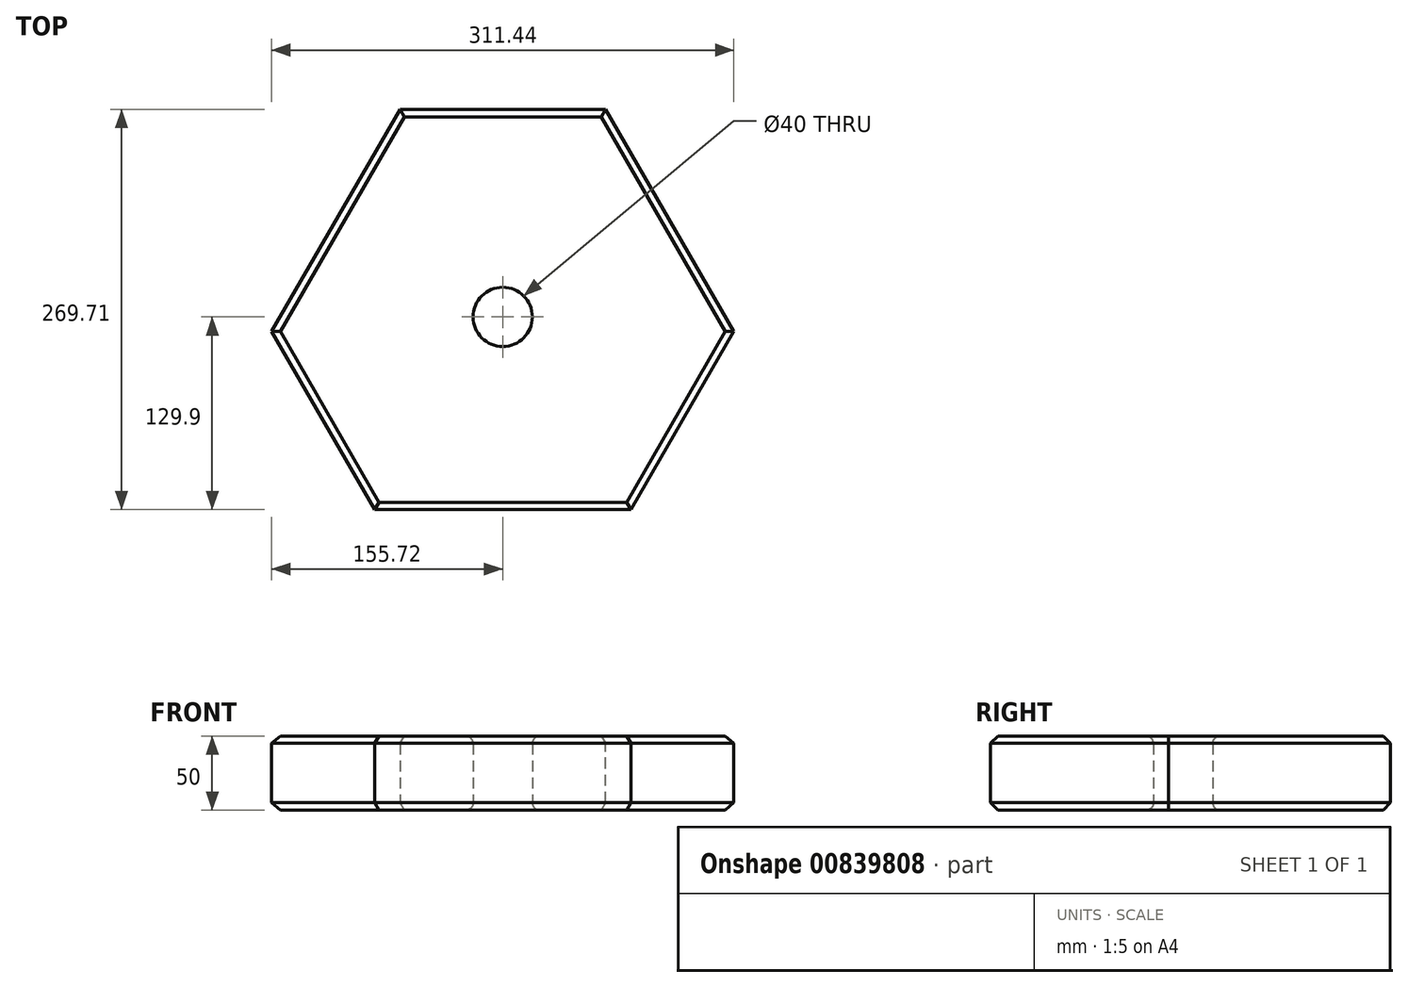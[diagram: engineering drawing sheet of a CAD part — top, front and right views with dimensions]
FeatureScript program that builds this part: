
annotation { "Feature Type Name" : "Feature", "Feature Type Description" : "" }
export const myFeature = defineFeature(function(context is Context, id is Id, definition is map)
    precondition{}
    {
        {
            var Q0;
            Q0=qCreatedBy(makeId("Top.planeOp"),FACE);
            var sketch = newSketch(context, id + "F0", { "sketchPlane" : qUnion([Q0])});
            skLineSegment(sketch, "E0", {"start": v(-225, -92.35) * mm, "end": v(0, 297.36) * mm});
            skLineSegment(sketch, "E1", {"start": v(0, 297.36) * mm, "end": v(225, -92.35) * mm});
            skLineSegment(sketch, "E2", {"start": v(225, -92.35) * mm, "end": v(-225, -92.35) * mm});
            skCircle(sketch, "E3", {"center": v(0, 37.55) * mm, "radius": 20 * mm});
            skPoint(sketch, "E4.orphan", {"position": v(-112.5, 102.5) * mm});
            skPoint(sketch, "E5.orphan", {"position": v(112.5, 102.5) * mm});
            skPoint(sketch, "E6.orphan", {"position": v(0, -92.35) * mm});
            skPoint(sketch, "E7.orphan", {"position": v(56.25, 5.07) * mm});
            skPoint(sketch, "E8.end.orphan", {"position": v(-56.25, 5.07) * mm});
            skPoint(sketch, "E9.end.orphan", {"position": v(0, 102.5) * mm});
            skSolve(sketch);
        }
        {
            var Q0;
            Q0=makeQuery(id+"F0.imprint","IMPRINT",FACE,{"disambiguationData":[TD([[makeQuery(id+"F0.imprint","IMPRINT",EDGE,{"derivedFrom":sQuery(id+"F0.wireOp",EDGE,"E0")}),-1.0]])]});
            extrude(context, id + "F1", {"entities" : qUnion([Q0]), "depth" : 50 * mm, "offsetDistance" : 25 * mm});
        }
        {
            var Q0;
            Q0=makeQuery(id+"F1.opExtrude","SWEPT_EDGE",EDGE,{"disambiguationData":[OSD([sQuery(id+"F0.wireOp",EDGE,"E1"),sQuery(id+"F0.wireOp",EDGE,"E2")])]});
            var Q1;
            Q1=makeQuery(id+"F1.opExtrude","SWEPT_EDGE",EDGE,{"disambiguationData":[OSD([sQuery(id+"F0.wireOp",EDGE,"E0"),sQuery(id+"F0.wireOp",EDGE,"E2")])]});
            var Q2;
            Q2=makeQuery(id+"F1.opExtrude","SWEPT_EDGE",EDGE,{"disambiguationData":[OSD([sQuery(id+"F0.wireOp",EDGE,"E0"),sQuery(id+"F0.wireOp",EDGE,"E1")])]});
            chamfer(context, id + "F2", {"entities" : qUnion([Q0, Q1, Q2]), "width" : 80 * mm, "tangentPropagation" : true});
        }
        {
            var Q0;
            Q0=makeQuery(id+"F1.opExtrude","CAP_EDGE",EDGE,{"disambiguationData":[OSD([sQuery(id+"F0.wireOp",EDGE,"E3")])],"isStart":false});
            var Q1;
            Q1=makeQuery(id+"F1.opExtrude","CAP_EDGE",EDGE,{"disambiguationData":[OSD([sQuery(id+"F0.wireOp",EDGE,"E3")])],"isStart":true});
            fillet(context, id + "F3", {"entities" : qUnion([Q0, Q1]), "radius" : 5 * mm, "tangentPropagation" : true, "allowEdgeOverflow" : false});
        }
        {
            var Q0;
            Q0=makeQuery(id+"F1.opExtrude","CAP_EDGE",EDGE,{"disambiguationData":[OSD([sQuery(id+"F0.wireOp",EDGE,"E1")])],"isStart":false});
            var Q1;
            {var subQ0=sQuery(id+"F0.wireOp",EDGE,"E2");var subQ1=sQuery(id+"F0.wireOp",EDGE,"E1");Q1=makeQuery(id+"F2.opChamfer","BLEND_EDGE",EDGE,{"blendedFrom":[makeQuery(id+"F1.opExtrude","SWEPT_EDGE",EDGE,{"disambiguationData":[OSD([subQ1,subQ0])]}),makeQuery(id+"F1.opExtrude","CAP_FACE",FACE,{"disambiguationData":[OSD([sQuery(id+"F0.wireOp",EDGE,"E0"),subQ1,subQ0,sQuery(id+"F0.wireOp",EDGE,"E3")])],"isStart":false})],"blendedInto":[makeQuery(id+"F1.opExtrude","CAP_FACE",FACE,{"disambiguationData":[OSD([sQuery(id+"F0.wireOp",EDGE,"E0"),subQ1,subQ0,sQuery(id+"F0.wireOp",EDGE,"E3")])],"isStart":false})]});}
            var Q2;
            Q2=makeQuery(id+"F1.opExtrude","CAP_EDGE",EDGE,{"disambiguationData":[OSD([sQuery(id+"F0.wireOp",EDGE,"E2")])],"isStart":false});
            var Q3;
            {var subQ0=sQuery(id+"F0.wireOp",EDGE,"E2");var subQ1=sQuery(id+"F0.wireOp",EDGE,"E0");Q3=makeQuery(id+"F2.opChamfer","BLEND_EDGE",EDGE,{"blendedFrom":[makeQuery(id+"F1.opExtrude","SWEPT_EDGE",EDGE,{"disambiguationData":[OSD([subQ1,subQ0])]}),makeQuery(id+"F1.opExtrude","CAP_FACE",FACE,{"disambiguationData":[OSD([subQ1,sQuery(id+"F0.wireOp",EDGE,"E1"),subQ0,sQuery(id+"F0.wireOp",EDGE,"E3")])],"isStart":false})],"blendedInto":[makeQuery(id+"F1.opExtrude","CAP_FACE",FACE,{"disambiguationData":[OSD([subQ1,sQuery(id+"F0.wireOp",EDGE,"E1"),subQ0,sQuery(id+"F0.wireOp",EDGE,"E3")])],"isStart":false})]});}
            var Q4;
            Q4=makeQuery(id+"F1.opExtrude","CAP_EDGE",EDGE,{"disambiguationData":[OSD([sQuery(id+"F0.wireOp",EDGE,"E0")])],"isStart":false});
            var Q5;
            {var subQ0=sQuery(id+"F0.wireOp",EDGE,"E2");var subQ1=sQuery(id+"F0.wireOp",EDGE,"E1");Q5=makeQuery(id+"F2.opChamfer","BLEND_EDGE",EDGE,{"blendedFrom":[makeQuery(id+"F1.opExtrude","SWEPT_EDGE",EDGE,{"disambiguationData":[OSD([subQ1,subQ0])]}),makeQuery(id+"F1.opExtrude","CAP_FACE",FACE,{"disambiguationData":[OSD([sQuery(id+"F0.wireOp",EDGE,"E0"),subQ1,subQ0,sQuery(id+"F0.wireOp",EDGE,"E3")])],"isStart":true})],"blendedInto":[makeQuery(id+"F1.opExtrude","CAP_FACE",FACE,{"disambiguationData":[OSD([sQuery(id+"F0.wireOp",EDGE,"E0"),subQ1,subQ0,sQuery(id+"F0.wireOp",EDGE,"E3")])],"isStart":true})]});}
            var Q6;
            Q6=makeQuery(id+"F1.opExtrude","CAP_EDGE",EDGE,{"disambiguationData":[OSD([sQuery(id+"F0.wireOp",EDGE,"E2")])],"isStart":true});
            var Q7;
            Q7=makeQuery(id+"F1.opExtrude","CAP_EDGE",EDGE,{"disambiguationData":[OSD([sQuery(id+"F0.wireOp",EDGE,"E1")])],"isStart":true});
            var Q8;
            {var subQ0=sQuery(id+"F0.wireOp",EDGE,"E2");var subQ1=sQuery(id+"F0.wireOp",EDGE,"E0");Q8=makeQuery(id+"F2.opChamfer","BLEND_EDGE",EDGE,{"blendedFrom":[makeQuery(id+"F1.opExtrude","SWEPT_EDGE",EDGE,{"disambiguationData":[OSD([subQ1,subQ0])]}),makeQuery(id+"F1.opExtrude","CAP_FACE",FACE,{"disambiguationData":[OSD([subQ1,sQuery(id+"F0.wireOp",EDGE,"E1"),subQ0,sQuery(id+"F0.wireOp",EDGE,"E3")])],"isStart":true})],"blendedInto":[makeQuery(id+"F1.opExtrude","CAP_FACE",FACE,{"disambiguationData":[OSD([subQ1,sQuery(id+"F0.wireOp",EDGE,"E1"),subQ0,sQuery(id+"F0.wireOp",EDGE,"E3")])],"isStart":true})]});}
            var Q9;
            Q9=makeQuery(id+"F1.opExtrude","CAP_EDGE",EDGE,{"disambiguationData":[OSD([sQuery(id+"F0.wireOp",EDGE,"E0")])],"isStart":true});
            var Q10;
            {var subQ0=sQuery(id+"F0.wireOp",EDGE,"E1");var subQ1=sQuery(id+"F0.wireOp",EDGE,"E0");Q10=makeQuery(id+"F2.opChamfer","BLEND_EDGE",EDGE,{"blendedFrom":[makeQuery(id+"F1.opExtrude","SWEPT_EDGE",EDGE,{"disambiguationData":[OSD([subQ1,subQ0])]}),makeQuery(id+"F1.opExtrude","CAP_FACE",FACE,{"disambiguationData":[OSD([subQ1,subQ0,sQuery(id+"F0.wireOp",EDGE,"E2"),sQuery(id+"F0.wireOp",EDGE,"E3")])],"isStart":true})],"blendedInto":[makeQuery(id+"F1.opExtrude","CAP_FACE",FACE,{"disambiguationData":[OSD([subQ1,subQ0,sQuery(id+"F0.wireOp",EDGE,"E2"),sQuery(id+"F0.wireOp",EDGE,"E3")])],"isStart":true})]});}
            var Q11;
            {var subQ0=sQuery(id+"F0.wireOp",EDGE,"E1");var subQ1=sQuery(id+"F0.wireOp",EDGE,"E0");Q11=makeQuery(id+"F2.opChamfer","BLEND_EDGE",EDGE,{"blendedFrom":[makeQuery(id+"F1.opExtrude","SWEPT_EDGE",EDGE,{"disambiguationData":[OSD([subQ1,subQ0])]}),makeQuery(id+"F1.opExtrude","CAP_FACE",FACE,{"disambiguationData":[OSD([subQ1,subQ0,sQuery(id+"F0.wireOp",EDGE,"E2"),sQuery(id+"F0.wireOp",EDGE,"E3")])],"isStart":false})],"blendedInto":[makeQuery(id+"F1.opExtrude","CAP_FACE",FACE,{"disambiguationData":[OSD([subQ1,subQ0,sQuery(id+"F0.wireOp",EDGE,"E2"),sQuery(id+"F0.wireOp",EDGE,"E3")])],"isStart":false})]});}
            chamfer(context, id + "F4", {"entities" : qUnion([Q0, Q1, Q2, Q3, Q4, Q5, Q6, Q7, Q8, Q9, Q10, Q11]), "width" : 5 * mm, "tangentPropagation" : true});
        }
    });
